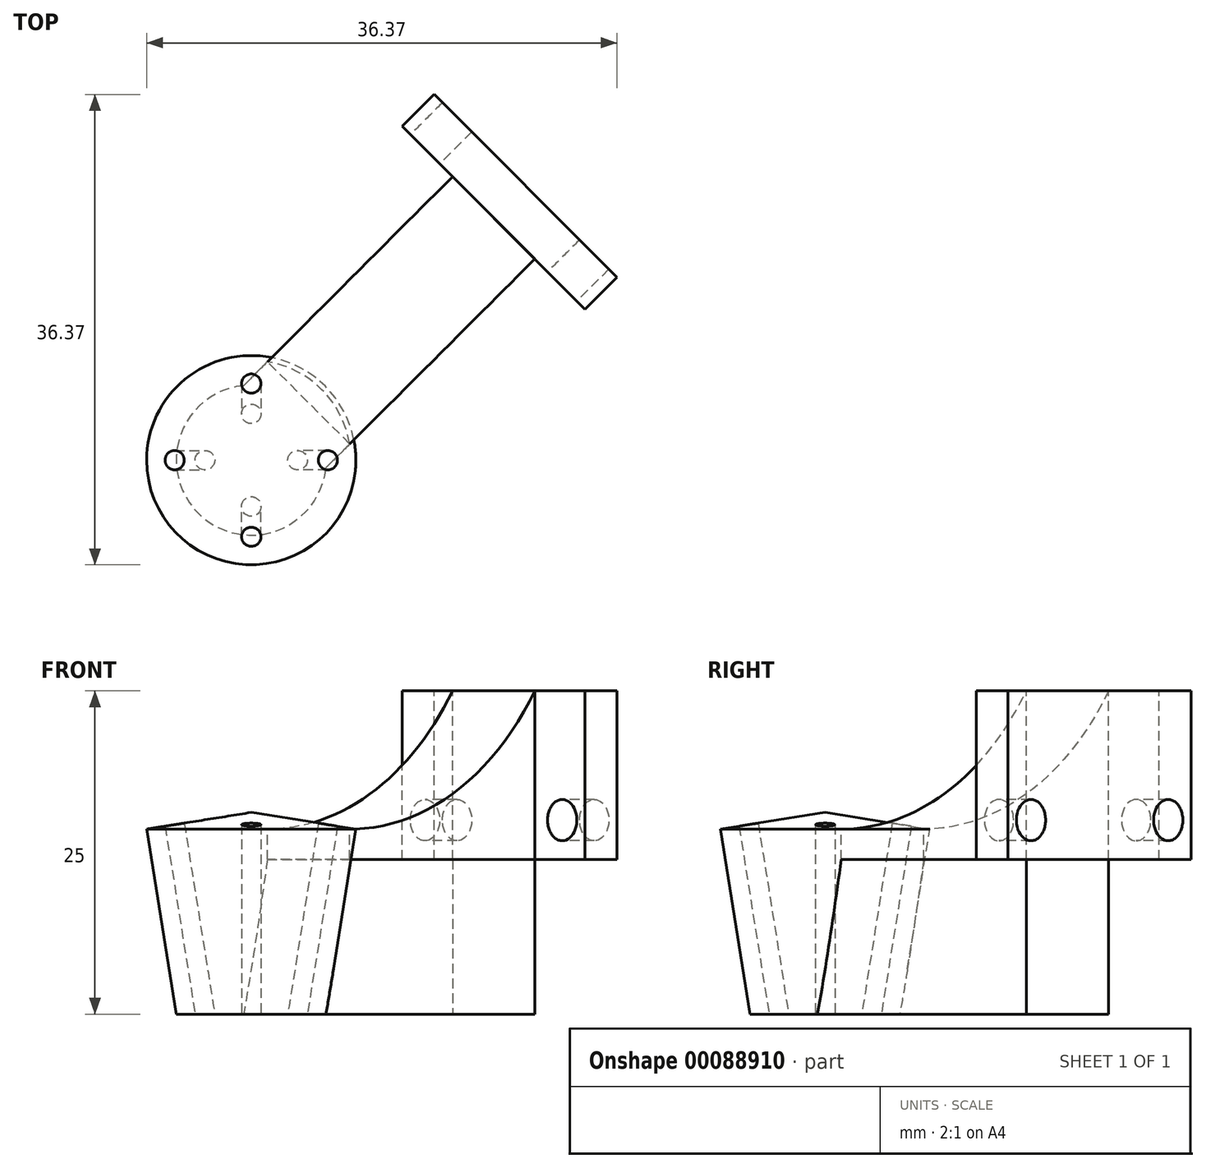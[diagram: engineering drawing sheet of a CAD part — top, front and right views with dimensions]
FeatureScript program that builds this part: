
annotation { "Feature Type Name" : "Feature", "Feature Type Description" : "" }
export const myFeature = defineFeature(function(context is Context, id is Id, definition is map)
    precondition{}
    {
        {
            var Q0;
            Q0=qCreatedBy(makeId("Front.planeOp"),FACE);
            var sketch = newSketch(context, id + "F0", { "sketchPlane" : qUnion([Q0])});
            skLineSegment(sketch, "E0", {"start": v(0, 0) * mm, "end": v(5.92, 37.02) * mm, "construction": true});
            skLineSegment(sketch, "E1", {"start": v(0, 0) * mm, "end": v(0, 51.82) * mm, "construction": true});
            skLineSegment(sketch, "E2", {"start": v(0, 37.97) * mm, "end": v(11.85, 36.07) * mm, "construction": true});
            skLineSegment(sketch, "E3", {"start": v(-4, 9.37) * mm, "end": v(4, 9.37) * mm, "construction": true});
            skPoint(sketch, "E4", {"position": v(1.5, 9.37) * mm});
            skLineSegment(sketch, "E5", {"start": v(5.18, 37.14) * mm, "end": v(0.74, 9.37) * mm});
            skLineSegment(sketch, "E6", {"start": v(0.74, 9.37) * mm, "end": v(1.48, 9.25) * mm});
            skLineSegment(sketch, "E7", {"start": v(1.48, 9.25) * mm, "end": v(5.92, 37.02) * mm});
            skLineSegment(sketch, "E8", {"start": v(5.18, 37.14) * mm, "end": v(5.92, 37.02) * mm});
            skSolve(sketch);
        }
        {
            var Q0;
            Q0=sQuery(id+"F0.wireOp",VERTEX,"E8.end");
            var Q1;
            Q1=qCreatedBy(makeId("Top.planeOp"),FACE);
            cPlane(context, id + "F1", {"entities" : qUnion([Q0, Q1]), "cplaneType" : CPlaneType.PLANE_POINT, "offset" : 25 * mm, "width" : 150 * mm, "height" : 150 * mm});
        }
        {
            var Q0;
            Q0=makeQuery(id+"F0.imprint","IMPRINT",FACE,{"disambiguationData":[TD([[makeQuery(id+"F0.imprint","IMPRINT",EDGE,{"derivedFrom":sQuery(id+"F0.wireOp",EDGE,"E5")}),1.0]])]});
            var Q1;
            Q1=sQuery(id+"F0.wireOp",EDGE,"E0");
            revolve(context, id + "F2", {"entities" : qUnion([Q0]), "axis" : qUnion([Q1]), "revolveType" : RevolveType.FULL});
        }
        {
            var Q0;
            Q0=makeQuery(id+"F2.opRevolve","SWEPT_BODY",BODY,{"disambiguationData":[OSD([sQuery(id+"F0.wireOp",EDGE,"E5"),sQuery(id+"F0.wireOp",EDGE,"E6"),sQuery(id+"F0.wireOp",EDGE,"E7"),sQuery(id+"F0.wireOp",EDGE,"E8")])]});
            var Q1;
            Q1=sQuery(id+"F0.wireOp",EDGE,"E1");
            circularPattern(context, id + "F3", {"entities" : qUnion([Q0]), "axis" : qUnion([Q1]), "angle" : 360 * degree, "instanceCount" : 4, "equalSpace" : true});
        }
        {
            var Q0;
            Q0=qCreatedBy(makeId("Front.planeOp"),FACE);
            var sketch = newSketch(context, id + "F4", { "sketchPlane" : qUnion([Q0])});
            skLineSegment(sketch, "E9", {"start": v(0, 37.97) * mm, "end": v(8.09, 36.67) * mm});
            skLineSegment(sketch, "E10", {"start": v(8.09, 36.67) * mm, "end": v(5, 17.37) * mm});
            skLineSegment(sketch, "E11", {"start": v(5, 17.37) * mm, "end": v(0, 17.37) * mm});
            skLineSegment(sketch, "E12", {"start": v(0, 17.37) * mm, "end": v(0, 37.97) * mm});
            skSolve(sketch);
        }
        {
            var Q0;
            Q0=qSketchRegion(id+"F4",true);
            var Q1;
            Q1=sQuery(id+"F0.wireOp",EDGE,"E1");
            revolve(context, id + "F5", {"entities" : qUnion([Q0]), "axis" : qUnion([Q1]), "revolveType" : RevolveType.FULL});
        }
        {
            var Q0;
            Q0=makeQuery(id+"F2.opRevolve","SWEPT_BODY",BODY,{"disambiguationData":[OSD([sQuery(id+"F0.wireOp",EDGE,"E5"),sQuery(id+"F0.wireOp",EDGE,"E6"),sQuery(id+"F0.wireOp",EDGE,"E7"),sQuery(id+"F0.wireOp",EDGE,"E8")])]});
            var Q1;
            Q1=makeQuery(id+"F3.opPattern","COPY",BODY,{"derivedFrom":makeQuery(id+"F2.opRevolve","SWEPT_BODY",BODY,{"disambiguationData":[OSD([sQuery(id+"F0.wireOp",EDGE,"E5"),sQuery(id+"F0.wireOp",EDGE,"E6"),sQuery(id+"F0.wireOp",EDGE,"E7"),sQuery(id+"F0.wireOp",EDGE,"E8")])]}),"instanceName":"1"});
            var Q2;
            Q2=makeQuery(id+"F3.opPattern","COPY",BODY,{"derivedFrom":makeQuery(id+"F2.opRevolve","SWEPT_BODY",BODY,{"disambiguationData":[OSD([sQuery(id+"F0.wireOp",EDGE,"E5"),sQuery(id+"F0.wireOp",EDGE,"E6"),sQuery(id+"F0.wireOp",EDGE,"E7"),sQuery(id+"F0.wireOp",EDGE,"E8")])]}),"instanceName":"2"});
            var Q3;
            Q3=makeQuery(id+"F3.opPattern","COPY",BODY,{"derivedFrom":makeQuery(id+"F2.opRevolve","SWEPT_BODY",BODY,{"disambiguationData":[OSD([sQuery(id+"F0.wireOp",EDGE,"E5"),sQuery(id+"F0.wireOp",EDGE,"E6"),sQuery(id+"F0.wireOp",EDGE,"E7"),sQuery(id+"F0.wireOp",EDGE,"E8")])]}),"instanceName":"3"});
            var Q4;
            Q4=makeQuery(id+"F3.opPattern","COPY",BODY,{"derivedFrom":makeQuery(id+"F2.opRevolve","SWEPT_BODY",BODY,{"disambiguationData":[OSD([sQuery(id+"F0.wireOp",EDGE,"E5"),sQuery(id+"F0.wireOp",EDGE,"E6"),sQuery(id+"F0.wireOp",EDGE,"E7"),sQuery(id+"F0.wireOp",EDGE,"E8")])]}),"instanceName":"4"});
            var Q5;
            Q5=makeQuery(id+"F3.opPattern","COPY",BODY,{"derivedFrom":makeQuery(id+"F2.opRevolve","SWEPT_BODY",BODY,{"disambiguationData":[OSD([sQuery(id+"F0.wireOp",EDGE,"E5"),sQuery(id+"F0.wireOp",EDGE,"E6"),sQuery(id+"F0.wireOp",EDGE,"E7"),sQuery(id+"F0.wireOp",EDGE,"E8")])]}),"instanceName":"5"});
            var Q6;
            Q6=makeQuery(id+"F3.opPattern","COPY",BODY,{"derivedFrom":makeQuery(id+"F2.opRevolve","SWEPT_BODY",BODY,{"disambiguationData":[OSD([sQuery(id+"F0.wireOp",EDGE,"E5"),sQuery(id+"F0.wireOp",EDGE,"E6"),sQuery(id+"F0.wireOp",EDGE,"E7"),sQuery(id+"F0.wireOp",EDGE,"E8")])]}),"instanceName":"6"});
            var Q7;
            Q7=makeQuery(id+"F3.opPattern","COPY",BODY,{"derivedFrom":makeQuery(id+"F2.opRevolve","SWEPT_BODY",BODY,{"disambiguationData":[OSD([sQuery(id+"F0.wireOp",EDGE,"E5"),sQuery(id+"F0.wireOp",EDGE,"E6"),sQuery(id+"F0.wireOp",EDGE,"E7"),sQuery(id+"F0.wireOp",EDGE,"E8")])]}),"instanceName":"7"});
            var Q8;
            Q8=makeQuery(id+"F5.opRevolve","SWEPT_BODY",BODY,{"disambiguationData":[OSD([sQuery(id+"F4.wireOp",EDGE,"E9"),sQuery(id+"F4.wireOp",EDGE,"E10"),sQuery(id+"F4.wireOp",EDGE,"E11"),sQuery(id+"F4.wireOp",EDGE,"E12")])]});
            booleanBodies(context, id + "F6", {"operationType" : BooleanOperationType.SUBTRACTION, "tools" : qUnion([Q0, Q1, Q2, Q3, Q4, Q5, Q6, Q7]), "targets" : qUnion([Q8])});
        }
        {
            var Q0;
            Q0=sQuery(id+"F0.wireOp",EDGE,"E1");
            cPlane(context, id + "F7", {"entities" : qUnion([Q0]), "cplaneType" : CPlaneType.LINE_ANGLE, "offset" : 25 * mm, "angle" : 45 * degree, "width" : 150 * mm, "height" : 150 * mm});
        }
        {
            var Q0;
            Q0=qCreatedBy(id+"F7.planeOp",FACE);
            cPlane(context, id + "F8", {"entities" : qUnion([Q0]), "cplaneType" : CPlaneType.OFFSET, "offset" : 30 * mm, "width" : 150 * mm, "height" : 150 * mm});
        }
        {
            var Q0;
            Q0=qCreatedBy(id+"F8.planeOp",FACE);
            cPlane(context, id + "F9", {"entities" : qUnion([Q0]), "cplaneType" : CPlaneType.OFFSET, "offset" : 3.5 * mm, "oppositeDirection" : true, "width" : 150 * mm, "height" : 150 * mm});
        }
        {
            var Q0;
            Q0=qCreatedBy(id+"F9.planeOp",FACE);
            var sketch = newSketch(context, id + "F10", { "sketchPlane" : qUnion([Q0])});
            skLineSegment(sketch, "E13.top", {"start": v(10, 47.37) * mm, "end": v(-10, 47.37) * mm});
            skLineSegment(sketch, "E13.left", {"start": v(10, 34.32) * mm, "end": v(10, 47.37) * mm});
            skLineSegment(sketch, "E13.right", {"start": v(-10, 34.32) * mm, "end": v(-10, 47.37) * mm});
            skLineSegment(sketch, "E14", {"start": v(-10, 34.32) * mm, "end": v(10, 34.32) * mm});
            skCircle(sketch, "E15", {"center": v(-7.5, 37.37) * mm, "radius": 1.6 * mm});
            skLineSegment(sketch, "E16", {"start": v(-15.33, 37.37) * mm, "end": v(20.16, 37.37) * mm, "construction": true});
            skCircle(sketch, "E17.MirrorC", {"center": v(7.5, 37.37) * mm, "radius": 1.6 * mm});
            skLineSegment(sketch, "E18", {"start": v(-4.5, 34.32) * mm, "end": v(-4.5, 17.37) * mm});
            skLineSegment(sketch, "E19.MirrorCS", {"start": v(4.5, 34.32) * mm, "end": v(4.5, 17.37) * mm});
            skPoint(sketch, "E20.end.orphan", {"position": v(0, 17.37) * mm});
            skLineSegment(sketch, "E21", {"start": v(-4.5, 17.37) * mm, "end": v(4.5, 17.37) * mm});
            skSolve(sketch);
        }
        {
            var Q0;
            Q0=makeQuery(id+"F10.imprint","IMPRINT",FACE,{"disambiguationData":[TD([[makeQuery(id+"F10.imprint","IMPRINT",EDGE,{"derivedFrom":sQuery(id+"F10.wireOp",EDGE,"E13.top")}),1.0]])]});
            var Q1;
            Q1=qCreatedBy(id+"F8.planeOp",FACE);
            extrude(context, id + "F11", {"entities" : qUnion([Q0]), "operationType" : NewBodyOperationType.ADD, "endBound" : BoundingType.UP_TO_SURFACE, "endBoundEntityFace" : qUnion([Q1]), "depth" : 25 * mm});
        }
        {
            var Q0;
            {var subQ0=sQuery(id+"F10.wireOp",EDGE,"E18");Q0=makeQuery(id+"F10.imprint","IMPRINT",FACE,{"disambiguationData":[TD([[makeQuery(id+"F10.imprint","IMPRINT",EDGE,{"derivedFrom":subQ0}),1.0]])]});}
            var Q1;
            Q1=makeQuery(id+"F5.opRevolve","SWEPT_FACE",FACE,{"disambiguationData":[OSD([sQuery(id+"F4.wireOp",EDGE,"E10")])]});
            extrude(context, id + "F12", {"entities" : qUnion([Q0]), "operationType" : NewBodyOperationType.ADD, "endBound" : BoundingType.UP_TO_SURFACE, "oppositeDirection" : true, "endBoundEntityFace" : qUnion([Q1]), "depth" : 25 * mm});
        }
        {
            var Q0;
            Q0=makeQuery(id+"F12.opExtrude","SWEPT_FACE",FACE,{"disambiguationData":[OSD([sQuery(id+"F10.wireOp",EDGE,"E19.MirrorCS")])]});
            var sketch = newSketch(context, id + "F13", { "sketchPlane" : qUnion([Q0])});
            skLineSegment(sketch, "E22", {"start": v(-26.5, 34.32) * mm, "end": v(-6.26, 34.32) * mm});
            skLineSegment(sketch, "E23", {"start": v(-26.5, 34.32) * mm, "end": v(-26.5, 47.37) * mm});
            skLineSegment(sketch, "E24", {"start": v(-6.26, 34.32) * mm, "end": v(-6.26, 36.67) * mm});
            skArc(sketch, "E25", {"start": v(-26.5, 47.37) * mm, "mid": v(-17.7, 39.51) * mm, "end": v(-6.26, 36.67) * mm});
            skLineSegment(sketch, "E26", {"start": v(-23.7, 36.67) * mm, "end": v(-17.76, 36.67) * mm, "construction": true});
            skSolve(sketch);
        }
        {
            var Q0;
            Q0=makeQuery(id+"F13.imprint","IMPRINT",FACE,{"disambiguationData":[TD([[makeQuery(id+"F13.imprint","IMPRINT",EDGE,{"derivedFrom":sQuery(id+"F13.wireOp",EDGE,"E22")}),-1.0]])]});
            var Q1;
            Q1=makeQuery(id+"F12.opExtrude","SWEPT_FACE",FACE,{"disambiguationData":[OSD([sQuery(id+"F10.wireOp",EDGE,"E18")])]});
            extrude(context, id + "F14", {"entities" : qUnion([Q0]), "endBound" : BoundingType.UP_TO_SURFACE, "oppositeDirection" : true, "endBoundEntityFace" : qUnion([Q1]), "depth" : 25 * mm});
        }
        {
            var Q0;
            {var subQ0=sQuery(id+"F10.wireOp",EDGE,"E18");Q0=makeQuery(id+"F10.imprint","IMPRINT",FACE,{"disambiguationData":[TD([[makeQuery(id+"F10.imprint","IMPRINT",EDGE,{"derivedFrom":subQ0}),1.0]])]});}
            var sketch = newSketch(context, id + "F15", { "sketchPlane" : qUnion([Q0])});
            skLineSegment(sketch, "E27.bottom", {"start": v(-10, 17.37) * mm, "end": v(10, 17.37) * mm});
            skLineSegment(sketch, "E27.top", {"start": v(-10, 22.37) * mm, "end": v(10, 22.37) * mm});
            skLineSegment(sketch, "E27.left", {"start": v(-10, 17.37) * mm, "end": v(-10, 22.37) * mm});
            skLineSegment(sketch, "E27.right", {"start": v(10, 17.37) * mm, "end": v(10, 22.37) * mm});
            skSolve(sketch);
        }
        {
            var Q0;
            Q0 = qSketchRegion(id + "F15", true);
            extrude(context, id + "F16", {"entities" : qUnion([Q0]), "operationType" : NewBodyOperationType.REMOVE, "endBound" : BoundingType.THROUGH_ALL, "oppositeDirection" : true, "depth" : 25 * mm});
        }
    });
